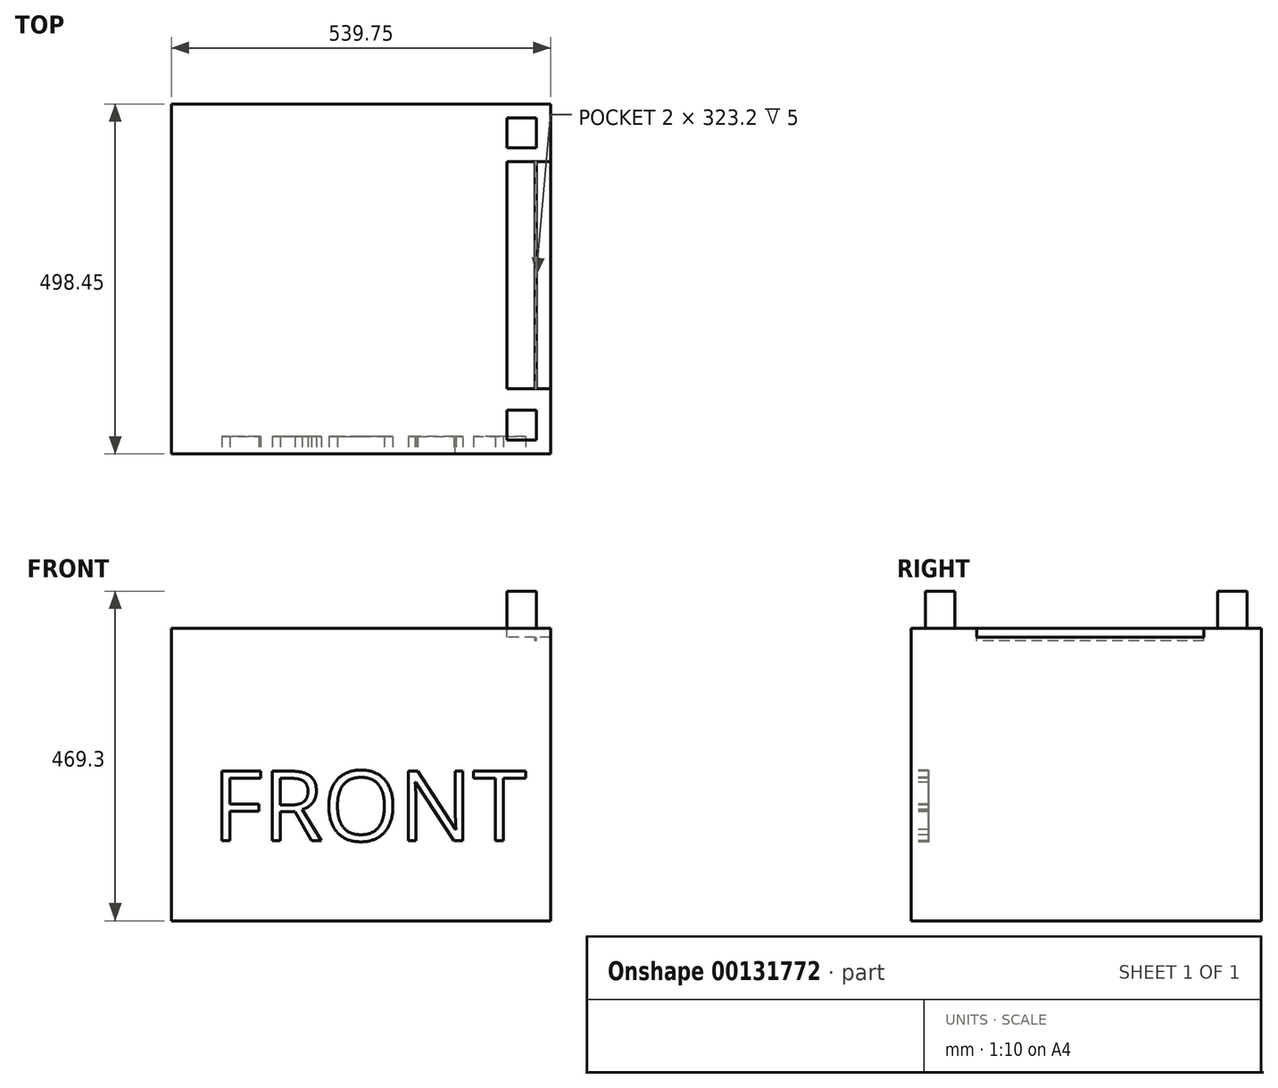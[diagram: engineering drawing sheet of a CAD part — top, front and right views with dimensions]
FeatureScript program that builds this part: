
annotation { "Feature Type Name" : "Feature", "Feature Type Description" : "" }
export const myFeature = defineFeature(function(context is Context, id is Id, definition is map)
    precondition{}
    {
        {
            var Q0;
            Q0=qCreatedBy(makeId("Top.planeOp"),FACE);
            var sketch = newSketch(context, id + "F0", { "sketchPlane" : qUnion([Q0])});
            skLineSegment(sketch, "E0.bottom", {"start": v(0, 0) * mm, "end": v(539.75, 0) * mm});
            skLineSegment(sketch, "E0.top", {"start": v(0, 498.45) * mm, "end": v(539.75, 498.45) * mm});
            skLineSegment(sketch, "E0.left", {"start": v(0, 0) * mm, "end": v(0, 498.45) * mm});
            skLineSegment(sketch, "E0.right", {"start": v(539.75, 0) * mm, "end": v(539.75, 498.45) * mm});
            skSolve(sketch);
        }
        {
            var Q0;
            Q0=makeQuery(id+"F0.imprint","IMPRINT",FACE,{"disambiguationData":[TD([[makeQuery(id+"F0.imprint","IMPRINT",EDGE,{"derivedFrom":sQuery(id+"F0.wireOp",EDGE,"E0.bottom")}),1.0]])]});
            extrude(context, id + "F1", {"entities" : qUnion([Q0]), "depth" : (17 * 24.5) * mm});
        }
        {
            var Q0;
            Q0=makeQuery(id+"F1.opExtrude","SWEPT_FACE",FACE,{"disambiguationData":[OSD([sQuery(id+"F0.wireOp",EDGE,"E0.bottom")])]});
            var sketch = newSketch(context, id + "F2", { "sketchPlane" : qUnion([Q0])});
            skText(sketch, "E1", { "text": "FRONT", "fontName": "OpenSans-Regular.ttf"});
            const initialGuessF2  = {"E1": [0.05813, 0.1138, 1, 0, 0.1]};
            skSetInitialGuess(sketch, initialGuessF2);
            skSolve(sketch);
        }
        {
            var Q0;
            Q0 = qSketchRegion(id + "F2", true);
            extrude(context, id + "F3", {"entities" : qUnion([Q0]), "operationType" : NewBodyOperationType.REMOVE, "oppositeDirection" : true, "depth" : 25 * mm});
        }
        {
            var Q0;
            Q0=makeQuery(id+"F1.opExtrude","CAP_FACE",FACE,{"disambiguationData":[OSD([sQuery(id+"F0.wireOp",EDGE,"E0.bottom"),sQuery(id+"F0.wireOp",EDGE,"E0.top"),sQuery(id+"F0.wireOp",EDGE,"E0.left"),sQuery(id+"F0.wireOp",EDGE,"E0.right")])],"isStart":false});
            var sketch = newSketch(context, id + "F4", { "sketchPlane" : qUnion([Q0])});
            skLineSegment(sketch, "E2.bottom", {"start": v(519.7, 20.05) * mm, "end": v(477.5, 20.05) * mm});
            skLineSegment(sketch, "E2.top", {"start": v(519.7, 62.25) * mm, "end": v(477.5, 62.25) * mm});
            skLineSegment(sketch, "E2.left", {"start": v(519.7, 20.05) * mm, "end": v(519.7, 62.25) * mm});
            skLineSegment(sketch, "E2.right", {"start": v(477.5, 20.05) * mm, "end": v(477.5, 62.25) * mm});
            skLineSegment(sketch, "E3.bottom", {"start": v(519.7, 478.4) * mm, "end": v(477.5, 478.4) * mm});
            skLineSegment(sketch, "E3.top", {"start": v(519.7, 436.2) * mm, "end": v(477.5, 436.2) * mm});
            skLineSegment(sketch, "E3.left", {"start": v(519.7, 478.4) * mm, "end": v(519.7, 436.2) * mm});
            skLineSegment(sketch, "E3.right", {"start": v(477.5, 478.4) * mm, "end": v(477.5, 436.2) * mm});
            skSolve(sketch);
        }
        {
            var Q0;
            Q0=makeQuery(id+"F4.imprint","IMPRINT",FACE,{"disambiguationData":[TD([[makeQuery(id+"F4.imprint","IMPRINT",EDGE,{"derivedFrom":sQuery(id+"F4.wireOp",EDGE,"E3.bottom")}),1.0]])]});
            var Q1;
            Q1=makeQuery(id+"F4.imprint","IMPRINT",FACE,{"disambiguationData":[TD([[makeQuery(id+"F4.imprint","IMPRINT",EDGE,{"derivedFrom":sQuery(id+"F4.wireOp",EDGE,"E2.bottom")}),-1.0]])]});
            extrude(context, id + "F5", {"entities" : qUnion([Q0, Q1]), "operationType" : NewBodyOperationType.ADD, "depth" : 52.8 * mm});
        }
        {
            var Q0;
            Q0=makeQuery(id+"F1.opExtrude","CAP_FACE",FACE,{"disambiguationData":[OSD([sQuery(id+"F0.wireOp",EDGE,"E0.bottom"),sQuery(id+"F0.wireOp",EDGE,"E0.top"),sQuery(id+"F0.wireOp",EDGE,"E0.left"),sQuery(id+"F0.wireOp",EDGE,"E0.right")])],"isStart":false});
            var sketch = newSketch(context, id + "F6", { "sketchPlane" : qUnion([Q0])});
            skLineSegment(sketch, "E4.bottom", {"start": v(539.75, 416.2) * mm, "end": v(477.5, 416.2) * mm});
            skLineSegment(sketch, "E4.top", {"start": v(539.75, 93) * mm, "end": v(477.5, 93) * mm});
            skLineSegment(sketch, "E4.left", {"start": v(539.75, 416.2) * mm, "end": v(539.75, 93) * mm});
            skLineSegment(sketch, "E4.right", {"start": v(477.5, 416.2) * mm, "end": v(477.5, 93) * mm});
            skSolve(sketch);
        }
        {
            var Q0;
            Q0=makeQuery(id+"F6.imprint","IMPRINT",FACE,{"disambiguationData":[TD([[makeQuery(id+"F6.imprint","IMPRINT",EDGE,{"derivedFrom":sQuery(id+"F6.wireOp",EDGE,"E4.bottom")}),1.0]])]});
            extrude(context, id + "F7", {"entities" : qUnion([Q0]), "operationType" : NewBodyOperationType.REMOVE, "oppositeDirection" : true, "depth" : 13 * mm});
        }
        {
            var Q0;
            Q0=makeQuery(id+"F7.boolean.opBoolean","COPY",FACE,{"derivedFrom":makeQuery(id+"F7.opExtrude","CAP_FACE",FACE,{"disambiguationData":[OSD([sQuery(id+"F6.wireOp",EDGE,"E4.bottom"),sQuery(id+"F6.wireOp",EDGE,"E4.top"),sQuery(id+"F6.wireOp",EDGE,"E4.left"),sQuery(id+"F6.wireOp",EDGE,"E4.right")])],"isStart":false})});
            var sketch = newSketch(context, id + "F8", { "sketchPlane" : qUnion([Q0])});
            skLineSegment(sketch, "E5.bottom", {"start": v(517.75, 416.2) * mm, "end": v(519.75, 416.2) * mm});
            skLineSegment(sketch, "E5.top", {"start": v(517.75, 93) * mm, "end": v(519.75, 93) * mm});
            skLineSegment(sketch, "E5.left", {"start": v(517.75, 416.2) * mm, "end": v(517.75, 93) * mm});
            skLineSegment(sketch, "E5.right", {"start": v(519.75, 416.2) * mm, "end": v(519.75, 93) * mm});
            skLineSegment(sketch, "E6", {"start": v(518.75, 416.2) * mm, "end": v(518.75, 93) * mm, "construction": true});
            skSolve(sketch);
        }
        {
            var Q0;
            Q0 = qSketchRegion(id + "F8", true);
            extrude(context, id + "F9", {"entities" : qUnion([Q0]), "operationType" : NewBodyOperationType.REMOVE, "oppositeDirection" : true, "depth" : 5 * mm});
        }
    });
